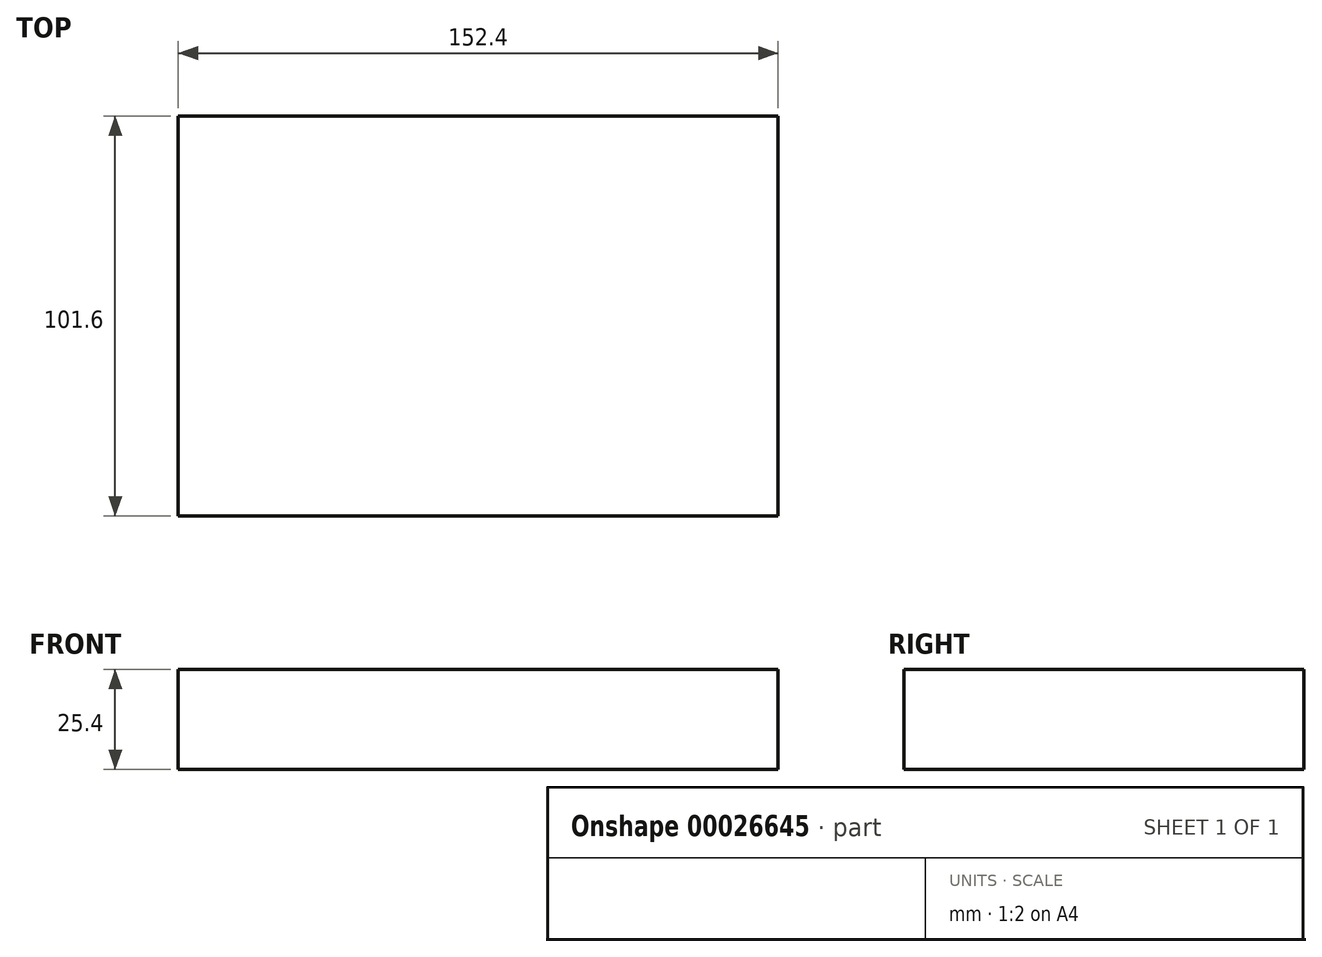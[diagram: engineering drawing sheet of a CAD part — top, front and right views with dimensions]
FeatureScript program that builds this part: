
annotation { "Feature Type Name" : "Feature", "Feature Type Description" : "" }
export const myFeature = defineFeature(function(context is Context, id is Id, definition is map)
    precondition{}
    {
        {
            var Q0;
            Q0=qCreatedBy(makeId("Top.planeOp"),FACE);
            var sketch = newSketch(context, id + "F0", { "sketchPlane" : qUnion([Q0])});
            skLineSegment(sketch, "E0.bottom", {"start": v(-76.2, 45.52) * mm, "end": v(76.2, 45.52) * mm});
            skLineSegment(sketch, "E0.top", {"start": v(-76.2, -56.08) * mm, "end": v(76.2, -56.08) * mm});
            skLineSegment(sketch, "E0.left", {"start": v(-76.2, 45.52) * mm, "end": v(-76.2, -56.08) * mm});
            skLineSegment(sketch, "E0.right", {"start": v(76.2, 45.52) * mm, "end": v(76.2, -56.08) * mm});
            skSolve(sketch);
        }
        {
            var Q0;
            Q0=makeQuery(id+"F0.imprint","IMPRINT",FACE,{"disambiguationData":[TD([[makeQuery(id+"F0.imprint","IMPRINT",EDGE,{"derivedFrom":sQuery(id+"F0.wireOp",EDGE,"E0.bottom")}),-1.0]])]});
            extrude(context, id + "F1", {"entities" : qUnion([Q0]), "depth" : 25.4 * mm});
        }
    });
